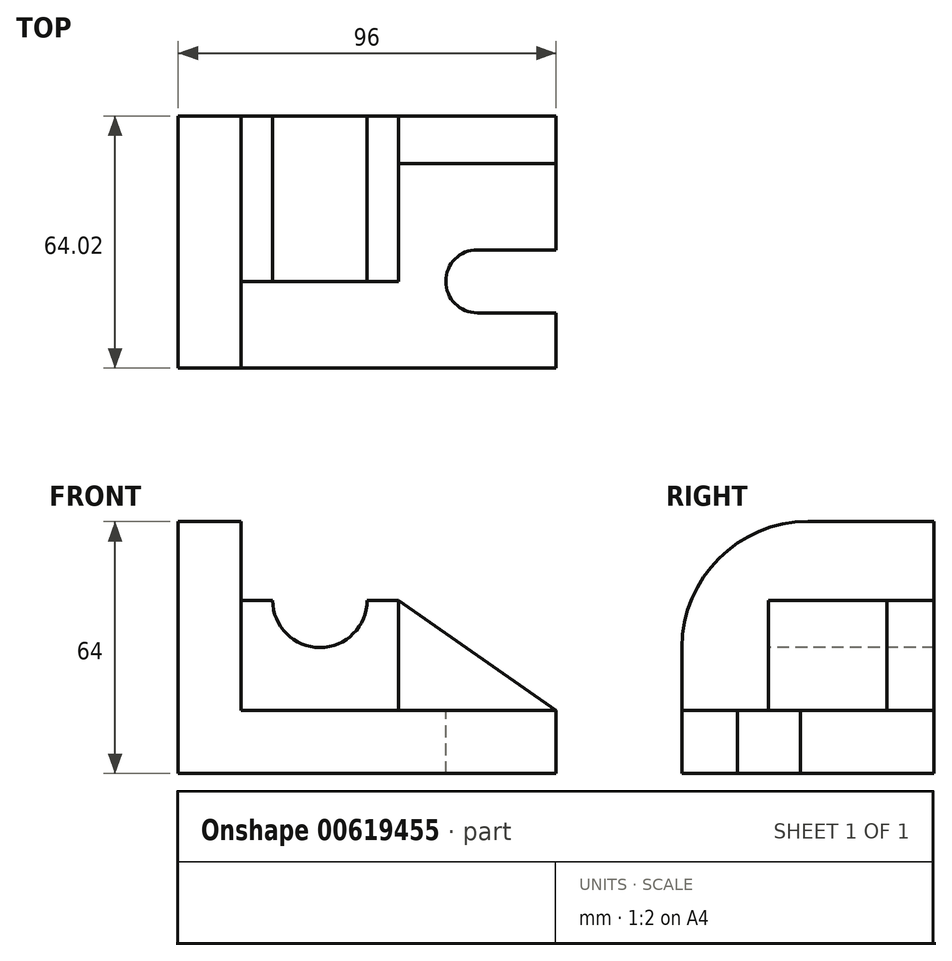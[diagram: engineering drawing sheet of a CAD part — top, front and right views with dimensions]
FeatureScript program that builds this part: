
annotation { "Feature Type Name" : "Feature", "Feature Type Description" : "" }
export const myFeature = defineFeature(function(context is Context, id is Id, definition is map)
    precondition{}
    {
        {
            var Q0;
            Q0=qCreatedBy(makeId("Top.planeOp"),FACE);
            var sketch = newSketch(context, id + "F0", { "sketchPlane" : qUnion([Q0])});
            skLineSegment(sketch, "E0.bottom", {"start": v(-48.34, 33.6) * mm, "end": v(47.66, 33.6) * mm});
            skLineSegment(sketch, "E0.top", {"start": v(-48.34, -30.4) * mm, "end": v(47.66, -30.4) * mm});
            skLineSegment(sketch, "E0.left", {"start": v(-48.34, 33.6) * mm, "end": v(-48.34, -30.4) * mm});
            skLineSegment(sketch, "E0.right", {"start": v(47.66, 33.6) * mm, "end": v(47.66, -30.4) * mm});
            skSolve(sketch);
        }
        {
            var Q0;
            Q0=makeQuery(id+"F0.imprint","IMPRINT",FACE,{"disambiguationData":[TD([[makeQuery(id+"F0.imprint","IMPRINT",EDGE,{"derivedFrom":sQuery(id+"F0.wireOp",EDGE,"E0.bottom")}),-1.0]])]});
            extrude(context, id + "F1", {"entities" : qUnion([Q0]), "depth" : 16 * mm, "offsetDistance" : 25.4 * mm});
        }
        {
            var Q0;
            Q0=makeQuery(id+"F1.opExtrude","CAP_FACE",FACE,{"disambiguationData":[OSD([sQuery(id+"F0.wireOp",EDGE,"E0.bottom"),sQuery(id+"F0.wireOp",EDGE,"E0.top"),sQuery(id+"F0.wireOp",EDGE,"E0.left"),sQuery(id+"F0.wireOp",EDGE,"E0.right")])],"isStart":false});
            var sketch = newSketch(context, id + "F2", { "sketchPlane" : qUnion([Q0])});
            skLineSegment(sketch, "E1.bottom", {"start": v(-48.34, -30.4) * mm, "end": v(-32.34, -30.4) * mm});
            skLineSegment(sketch, "E1.top", {"start": v(-48.34, 33.6) * mm, "end": v(-32.34, 33.6) * mm});
            skLineSegment(sketch, "E1.left", {"start": v(-48.34, -30.4) * mm, "end": v(-48.34, 33.6) * mm});
            skLineSegment(sketch, "E1.right", {"start": v(-32.34, -30.4) * mm, "end": v(-32.34, 33.6) * mm});
            skSolve(sketch);
        }
        {
            var Q0;
            Q0 = qSketchRegion(id + "F2", true);
            extrude(context, id + "F3", {"entities" : qUnion([Q0]), "operationType" : NewBodyOperationType.ADD, "depth" : 48 * mm, "offsetDistance" : 25.4 * mm});
        }
        {
            var Q0;
            Q0=makeQuery(id+"F3.opExtrude","CAP_EDGE",EDGE,{"disambiguationData":[OSD([sQuery(id+"F2.wireOp",EDGE,"E1.bottom")])],"isStart":false});
            fillet(context, id + "F4", {"entities" : qUnion([Q0]), "radius" : 32 * mm, "tangentPropagation" : true, "allowEdgeOverflow" : false});
        }
        {
            var Q0;
            Q0=makeQuery(id+"F1.opExtrude","CAP_FACE",FACE,{"disambiguationData":[OSD([sQuery(id+"F0.wireOp",EDGE,"E0.bottom"),sQuery(id+"F0.wireOp",EDGE,"E0.top"),sQuery(id+"F0.wireOp",EDGE,"E0.left"),sQuery(id+"F0.wireOp",EDGE,"E0.right")])],"isStart":false});
            var sketch = newSketch(context, id + "F5", { "sketchPlane" : qUnion([Q0])});
            skLineSegment(sketch, "E2.bottom", {"start": v(-32.34, 33.61) * mm, "end": v(7.66, 33.61) * mm});
            skLineSegment(sketch, "E2.top", {"start": v(-32.34, -8.39) * mm, "end": v(7.66, -8.39) * mm});
            skLineSegment(sketch, "E2.left", {"start": v(-32.34, 33.61) * mm, "end": v(-32.34, -8.39) * mm});
            skLineSegment(sketch, "E2.right", {"start": v(7.66, 33.61) * mm, "end": v(7.66, -8.39) * mm});
            skSolve(sketch);
        }
        {
            var Q0;
            Q0 = qSketchRegion(id + "F5", true);
            extrude(context, id + "F6", {"entities" : qUnion([Q0]), "operationType" : NewBodyOperationType.ADD, "depth" : 28 * mm, "offsetDistance" : 25.4 * mm});
        }
        {
            var Q0;
            Q0=makeQuery(id+"F1.opExtrude","CAP_FACE",FACE,{"disambiguationData":[OSD([sQuery(id+"F0.wireOp",EDGE,"E0.bottom"),sQuery(id+"F0.wireOp",EDGE,"E0.top"),sQuery(id+"F0.wireOp",EDGE,"E0.left"),sQuery(id+"F0.wireOp",EDGE,"E0.right")])],"isStart":false});
            var sketch = newSketch(context, id + "F7", { "sketchPlane" : qUnion([Q0])});
            skLineSegment(sketch, "E3.bottom", {"start": v(7.66, 33.6) * mm, "end": v(47.66, 33.6) * mm});
            skLineSegment(sketch, "E3.top", {"start": v(7.66, 21.6) * mm, "end": v(47.66, 21.6) * mm});
            skLineSegment(sketch, "E3.left", {"start": v(7.66, 33.6) * mm, "end": v(7.66, 21.6) * mm});
            skLineSegment(sketch, "E3.right", {"start": v(47.66, 33.6) * mm, "end": v(47.66, 21.6) * mm});
            skSolve(sketch);
        }
        {
            var Q0;
            Q0 = qSketchRegion(id + "F7", true);
            extrude(context, id + "F8", {"entities" : qUnion([Q0]), "operationType" : NewBodyOperationType.ADD, "depth" : 28 * mm, "offsetDistance" : 25.4 * mm});
        }
        {
            var Q0;
            Q0=makeQuery(id+"F8.opExtrude","SWEPT_FACE",FACE,{"disambiguationData":[OSD([sQuery(id+"F7.wireOp",EDGE,"E3.top")])]});
            var sketch = newSketch(context, id + "F9", { "sketchPlane" : qUnion([Q0])});
            skLineSegment(sketch, "E4", {"start": v(7.66, 44) * mm, "end": v(47.66, 16) * mm});
            skSolve(sketch);
        }
        {
            var Q0;
            Q0=makeQuery(id+"F9.imprint","IMPRINT",FACE,{"disambiguationData":[TD([[makeQuery(id+"F9.imprint","IMPRINT",EDGE,{"derivedFrom":sQuery(id+"F9.wireOp",EDGE,"E4")}),1.0]])]});
            extrude(context, id + "F10", {"entities" : qUnion([Q0]), "operationType" : NewBodyOperationType.REMOVE, "oppositeDirection" : true, "depth" : 25.4 * mm, "offsetDistance" : 25.4 * mm});
        }
        {
            var Q0;
            Q0=makeQuery(id+"F6.opExtrude","SWEPT_FACE",FACE,{"disambiguationData":[OSD([sQuery(id+"F5.wireOp",EDGE,"E2.top")])]});
            var sketch = newSketch(context, id + "F11", { "sketchPlane" : qUnion([Q0])});
            skCircle(sketch, "E5", {"center": v(-12.34, 44) * mm, "radius": 12 * mm});
            skSolve(sketch);
        }
        {
            var Q0;
            Q0 = qSketchRegion(id + "F11", true);
            extrude(context, id + "F12", {"entities" : qUnion([Q0]), "operationType" : NewBodyOperationType.REMOVE, "oppositeDirection" : true, "depth" : 63.25 * mm, "offsetDistance" : 25.4 * mm});
        }
        {
            var Q0;
            Q0=makeQuery(id+"F1.opExtrude","CAP_FACE",FACE,{"disambiguationData":[OSD([sQuery(id+"F0.wireOp",EDGE,"E0.bottom"),sQuery(id+"F0.wireOp",EDGE,"E0.top"),sQuery(id+"F0.wireOp",EDGE,"E0.left"),sQuery(id+"F0.wireOp",EDGE,"E0.right")])],"isStart":false});
            var sketch = newSketch(context, id + "F13", { "sketchPlane" : qUnion([Q0])});
            skLineSegment(sketch, "E6.bottom", {"start": v(27.66, -0.37) * mm, "end": v(47.66, -0.37) * mm});
            skLineSegment(sketch, "E6.top", {"start": v(27.66, -16.37) * mm, "end": v(47.66, -16.37) * mm});
            skLineSegment(sketch, "E6.left", {"start": v(27.66, -0.37) * mm, "end": v(27.66, -16.37) * mm});
            skLineSegment(sketch, "E6.right", {"start": v(47.66, -0.37) * mm, "end": v(47.66, -16.37) * mm});
            skCircle(sketch, "E7", {"center": v(27.66, -8.37) * mm, "radius": 8 * mm});
            skSolve(sketch);
        }
        {
            var Q0;
            Q0 = qSketchRegion(id + "F13", true);
            extrude(context, id + "F14", {"entities" : qUnion([Q0]), "operationType" : NewBodyOperationType.REMOVE, "oppositeDirection" : true, "depth" : 25.4 * mm, "offsetDistance" : 25.4 * mm});
        }
    });
